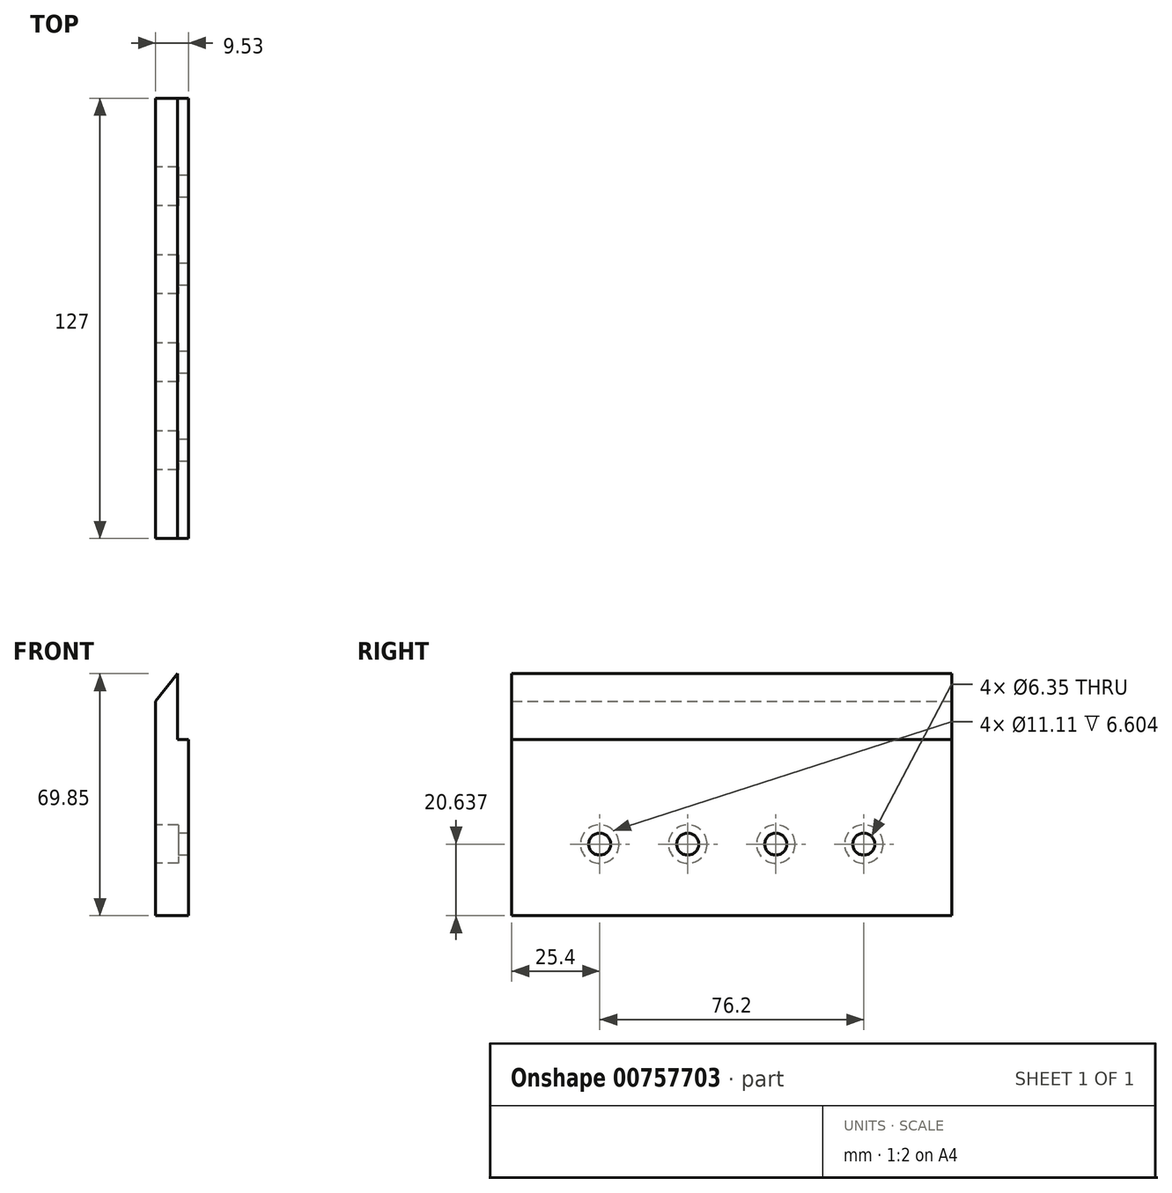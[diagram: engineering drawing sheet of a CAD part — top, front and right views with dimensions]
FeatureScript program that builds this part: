
annotation { "Feature Type Name" : "Feature", "Feature Type Description" : "" }
export const myFeature = defineFeature(function(context is Context, id is Id, definition is map)
    precondition{}
    {
        {
            var Q0;
            Q0=qCreatedBy(makeId("Front.planeOp"),FACE);
            var sketch = newSketch(context, id + "F0", { "sketchPlane" : qUnion([Q0])});
            skLineSegment(sketch, "E0", {"start": v(0, 0) * mm, "end": v(0, 61.91) * mm});
            skLineSegment(sketch, "E1", {"start": v(0, 61.91) * mm, "end": v(6.35, 69.85) * mm});
            skLineSegment(sketch, "E2", {"start": v(6.35, 69.85) * mm, "end": v(6.35, 50.8) * mm});
            skLineSegment(sketch, "E3", {"start": v(6.35, 50.8) * mm, "end": v(9.53, 50.8) * mm});
            skLineSegment(sketch, "E4", {"start": v(9.53, 50.8) * mm, "end": v(9.53, 0) * mm});
            skLineSegment(sketch, "E5", {"start": v(9.53, 0) * mm, "end": v(0, 0) * mm});
            skSolve(sketch);
        }
        {
            var Q0;
            Q0 = qSketchRegion(id + "F0", true);
            extrude(context, id + "F1", {"entities" : qUnion([Q0]), "depth" : 127 * mm, "offsetDistance" : 25.4 * mm});
        }
        {
            var Q0;
            Q0=makeQuery(id+"F1.opExtrude","SWEPT_FACE",FACE,{"disambiguationData":[OSD([sQuery(id+"F0.wireOp",EDGE,"E0")])]});
            var sketch = newSketch(context, id + "F2", { "sketchPlane" : qUnion([Q0])});
            skLineSegment(sketch, "E6", {"start": v(127, 0) * mm, "end": v(127, 20.64) * mm});
            skLineSegment(sketch, "E7", {"start": v(127, 20.64) * mm, "end": v(0, 20.64) * mm});
            skCircle(sketch, "E8", {"center": v(101.6, 20.64) * mm, "radius": 3.18 * mm});
            skCircle(sketch, "E9.1.0.0", {"center": v(76.2, 20.64) * mm, "radius": 3.18 * mm});
            skCircle(sketch, "E9.2.0.0", {"center": v(50.8, 20.64) * mm, "radius": 3.18 * mm});
            skCircle(sketch, "E9.3.0.0", {"center": v(25.4, 20.64) * mm, "radius": 3.18 * mm});
            skLineSegment(sketch, "E9.direction1", {"start": v(101.6, 20.64) * mm, "end": v(76.2, 20.64) * mm, "construction": true});
            skSolve(sketch);
        }
        {
            var Q0;
            Q0 = qSketchRegion(id + "F2", true);
            extrude(context, id + "F3", {"entities" : qUnion([Q0]), "operationType" : NewBodyOperationType.REMOVE, "oppositeDirection" : true, "depth" : 25.4 * mm, "offsetDistance" : 25.4 * mm});
        }
        {
            var Q0;
            Q0=makeQuery(id+"F1.opExtrude","SWEPT_FACE",FACE,{"disambiguationData":[OSD([sQuery(id+"F0.wireOp",EDGE,"E0")])]});
            var sketch = newSketch(context, id + "F4", { "sketchPlane" : qUnion([Q0])});
            skCircle(sketch, "E10", {"center": v(101.6, 20.64) * mm, "radius": 5.56 * mm});
            skCircle(sketch, "E11", {"center": v(76.2, 20.64) * mm, "radius": 5.56 * mm});
            skCircle(sketch, "E12", {"center": v(50.8, 20.64) * mm, "radius": 5.56 * mm});
            skCircle(sketch, "E13", {"center": v(25.4, 20.64) * mm, "radius": 5.56 * mm});
            skSolve(sketch);
        }
        {
            var Q0;
            Q0 = qSketchRegion(id + "F4", true);
            extrude(context, id + "F5", {"entities" : qUnion([Q0]), "operationType" : NewBodyOperationType.REMOVE, "oppositeDirection" : true, "depth" : 6.6 * mm, "offsetDistance" : 25.4 * mm});
        }
    });
